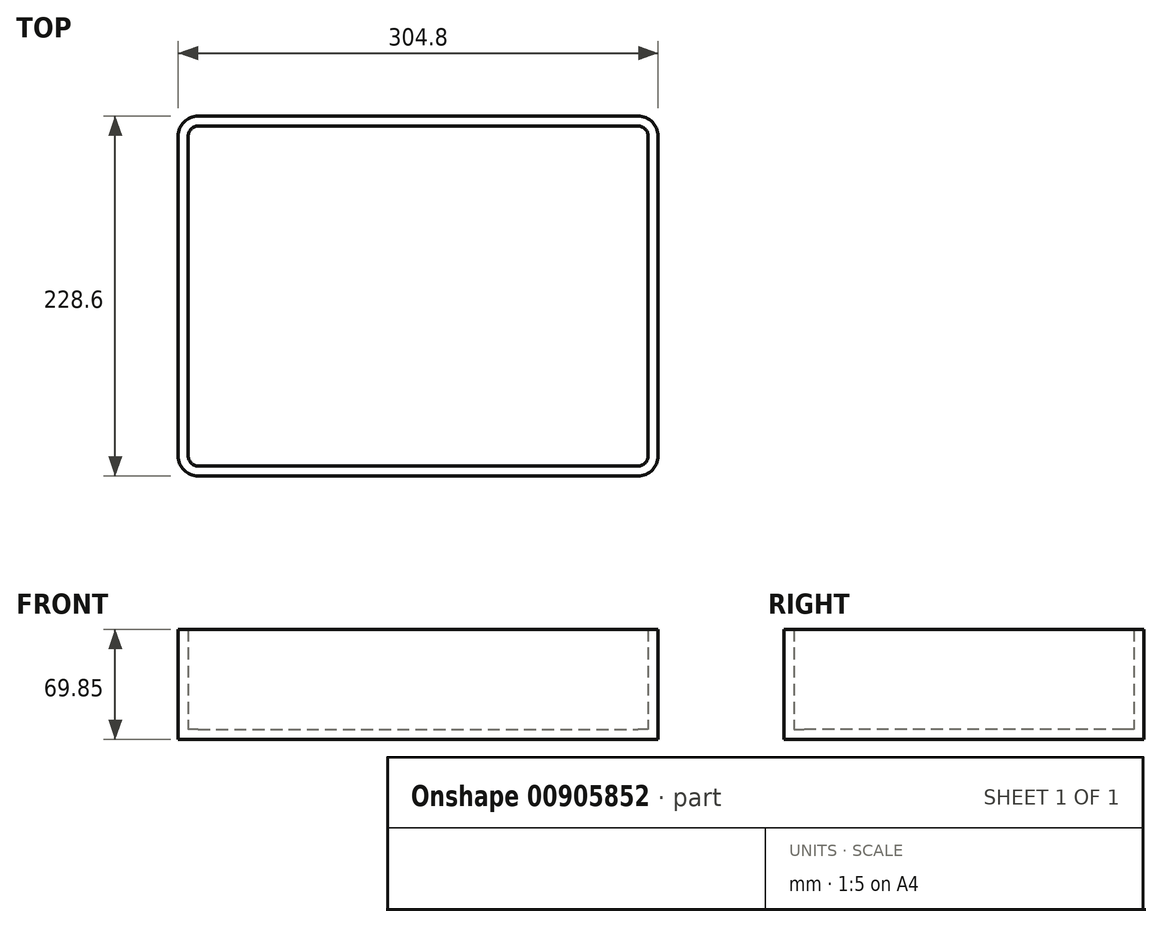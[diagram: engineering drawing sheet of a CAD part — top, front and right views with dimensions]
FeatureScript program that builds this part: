
annotation { "Feature Type Name" : "Feature", "Feature Type Description" : "" }
export const myFeature = defineFeature(function(context is Context, id is Id, definition is map)
    precondition{}
    {
        {
            var Q0;
            Q0=qCreatedBy(makeId("Top.planeOp"),FACE);
            var sketch = newSketch(context, id + "F0", { "sketchPlane" : qUnion([Q0])});
            skLineSegment(sketch, "E0.bottom", {"start": v(-139.7, 114.3) * mm, "end": v(139.7, 114.3) * mm});
            skLineSegment(sketch, "E0.top", {"start": v(-139.7, -114.3) * mm, "end": v(139.7, -114.3) * mm});
            skLineSegment(sketch, "E0.left", {"start": v(-152.4, 101.6) * mm, "end": v(-152.4, -101.6) * mm});
            skLineSegment(sketch, "E0.right", {"start": v(152.4, 101.6) * mm, "end": v(152.4, -101.6) * mm});
            skPoint(sketch, "E1.visualSharp", {"position": v(-152.4, 114.3) * mm});
            skArc(sketch, "E1.filletArc", {"start": v(-139.7, 114.3) * mm, "mid": v(-148.68, 110.58) * mm, "end": v(-152.4, 101.6) * mm});
            skPoint(sketch, "E2.visualSharp", {"position": v(152.4, 114.3) * mm});
            skArc(sketch, "E2.filletArc", {"start": v(152.4, 101.6) * mm, "mid": v(148.68, 110.58) * mm, "end": v(139.7, 114.3) * mm});
            skPoint(sketch, "E3.visualSharp", {"position": v(152.4, -114.3) * mm});
            skArc(sketch, "E3.filletArc", {"start": v(139.7, -114.3) * mm, "mid": v(148.68, -110.58) * mm, "end": v(152.4, -101.6) * mm});
            skPoint(sketch, "E4.visualSharp", {"position": v(-152.4, -114.3) * mm});
            skArc(sketch, "E4.filletArc", {"start": v(-152.4, -101.6) * mm, "mid": v(-148.68, -110.58) * mm, "end": v(-139.7, -114.3) * mm});
            skArc(sketch, "E5.0", {"start": v(-139.7, 107.95) * mm, "mid": v(-144.2, 106.1) * mm, "end": v(-146.05, 101.6) * mm});
            skLineSegment(sketch, "E5.1", {"start": v(-146.05, 101.6) * mm, "end": v(-146.05, -101.6) * mm});
            skLineSegment(sketch, "E5.2", {"start": v(-139.7, 107.95) * mm, "end": v(139.7, 107.95) * mm});
            skArc(sketch, "E5.3", {"start": v(-146.05, -101.6) * mm, "mid": v(-144.2, -106.1) * mm, "end": v(-139.7, -107.95) * mm});
            skArc(sketch, "E5.4", {"start": v(146.05, 101.6) * mm, "mid": v(144.2, 106.1) * mm, "end": v(139.7, 107.95) * mm});
            skLineSegment(sketch, "E5.5", {"start": v(146.05, 101.6) * mm, "end": v(146.05, -101.6) * mm});
            skArc(sketch, "E5.6", {"start": v(139.7, -107.95) * mm, "mid": v(144.2, -106.1) * mm, "end": v(146.05, -101.6) * mm});
            skLineSegment(sketch, "E5.7", {"start": v(-139.7, -107.95) * mm, "end": v(139.7, -107.95) * mm});
            skSolve(sketch);
        }
        {
            var Q0;
            Q0 = qSketchRegion(id + "F0", true);
            extrude(context, id + "F1", {"entities" : qUnion([Q0]), "depth" : 63.5 * mm, "offsetDistance" : 25.4 * mm});
        }
        {
            var Q0;
            Q0=qCreatedBy(makeId("Top.planeOp"),FACE);
            var sketch = newSketch(context, id + "F2", { "sketchPlane" : qUnion([Q0])});
            skLineSegment(sketch, "E6.bottom", {"start": v(-139.7, -114.3) * mm, "end": v(139.7, -114.3) * mm});
            skLineSegment(sketch, "E6.top", {"start": v(-139.7, 114.3) * mm, "end": v(139.7, 114.3) * mm});
            skLineSegment(sketch, "E6.left", {"start": v(-152.4, -101.6) * mm, "end": v(-152.4, 101.6) * mm});
            skLineSegment(sketch, "E6.right", {"start": v(152.4, -101.6) * mm, "end": v(152.4, 101.6) * mm});
            skPoint(sketch, "E7.visualSharp", {"position": v(-152.4, -114.3) * mm});
            skArc(sketch, "E7.filletArc", {"start": v(-152.4, -101.6) * mm, "mid": v(-148.68, -110.58) * mm, "end": v(-139.7, -114.3) * mm});
            skPoint(sketch, "E8.visualSharp", {"position": v(152.4, -114.3) * mm});
            skArc(sketch, "E8.filletArc", {"start": v(139.7, -114.3) * mm, "mid": v(148.68, -110.58) * mm, "end": v(152.4, -101.6) * mm});
            skPoint(sketch, "E9.visualSharp", {"position": v(152.4, 114.3) * mm});
            skArc(sketch, "E9.filletArc", {"start": v(152.4, 101.6) * mm, "mid": v(148.68, 110.58) * mm, "end": v(139.7, 114.3) * mm});
            skPoint(sketch, "E10.visualSharp", {"position": v(-152.4, 114.3) * mm});
            skArc(sketch, "E10.filletArc", {"start": v(-139.7, 114.3) * mm, "mid": v(-148.68, 110.58) * mm, "end": v(-152.4, 101.6) * mm});
            skSolve(sketch);
        }
        {
            var Q0;
            Q0 = qSketchRegion(id + "F2", true);
            extrude(context, id + "F3", {"entities" : qUnion([Q0]), "operationType" : NewBodyOperationType.ADD, "oppositeDirection" : true, "depth" : 6.35 * mm, "offsetDistance" : 25.4 * mm});
        }
    });
